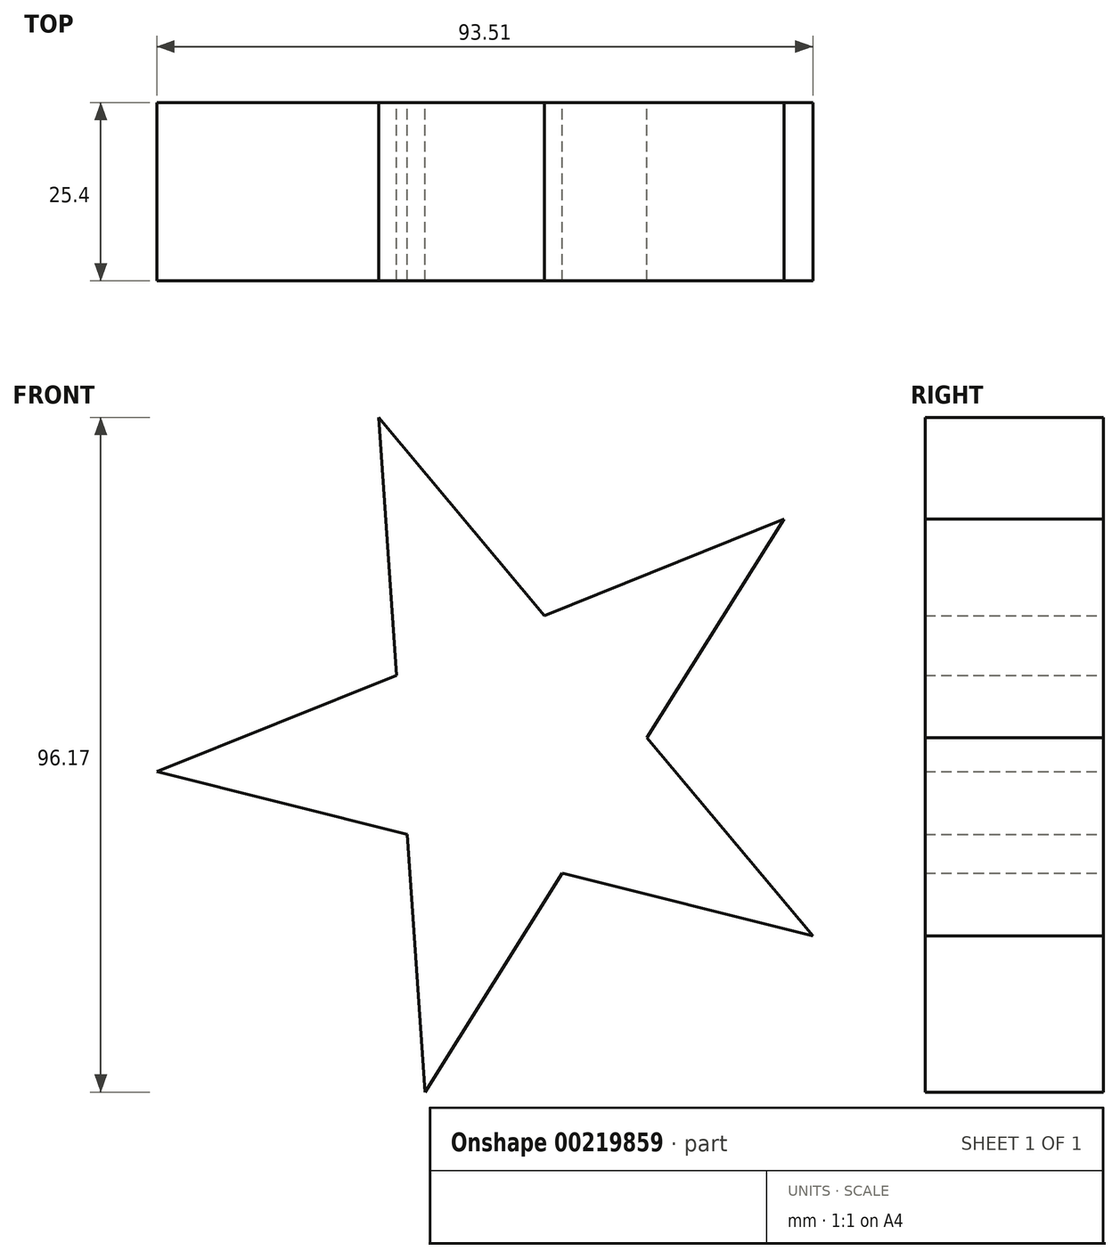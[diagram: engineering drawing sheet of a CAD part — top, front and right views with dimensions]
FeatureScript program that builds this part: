
annotation { "Feature Type Name" : "Feature", "Feature Type Description" : "" }
export const myFeature = defineFeature(function(context is Context, id is Id, definition is map)
    precondition{}
    {
        {
            var Q0;
            Q0=qCreatedBy(makeId("Front.planeOp"),FACE);
            var sketch = newSketch(context, id + "F0", { "sketchPlane" : qUnion([Q0])});
            skLineSegment(sketch, "E0", {"start": v(-18.93, 47) * mm, "end": v(-16.4, 10.28) * mm});
            skLineSegment(sketch, "E1", {"start": v(-12.31, -49.16) * mm, "end": v(7.23, -17.96) * mm});
            skLineSegment(sketch, "E2", {"start": v(-50.56, -3.48) * mm, "end": v(-16.4, 10.28) * mm});
            skLineSegment(sketch, "E3", {"start": v(42.95, -26.9) * mm, "end": v(7.23, -17.96) * mm});
            skLineSegment(sketch, "E4", {"start": v(42.95, -26.9) * mm, "end": v(19.31, 1.33) * mm});
            skLineSegment(sketch, "E5.trimOffspring", {"start": v(4.7, 18.78) * mm, "end": v(38.86, 32.53) * mm});
            skLineSegment(sketch, "E6.trimOffspring", {"start": v(-14.84, -12.43) * mm, "end": v(-12.31, -49.16) * mm});
            skLineSegment(sketch, "E7.trimOffspring", {"start": v(4.7, 18.78) * mm, "end": v(-18.93, 47) * mm});
            skLineSegment(sketch, "E8.trimOffspring", {"start": v(19.31, 1.33) * mm, "end": v(38.86, 32.53) * mm});
            skLineSegment(sketch, "E9.trimOffspring", {"start": v(-14.84, -12.43) * mm, "end": v(-50.56, -3.48) * mm});
            skSolve(sketch);
        }
        {
            var Q0;
            Q0=makeQuery(id+"F0.imprint","IMPRINT",FACE,{"disambiguationData":[TD([[makeQuery(id+"F0.imprint","IMPRINT",EDGE,{"derivedFrom":sQuery(id+"F0.wireOp",EDGE,"E0")}),1.0]])]});
            extrude(context, id + "F1", {"entities" : qUnion([Q0]), "depth" : 25.4 * mm});
        }
    });
